AUTODESK INVENTOR PART (.ipt)
format: ipt  version: 2015 (Build 190159000, 159)  size: 509,952 bytes
history: native  units: mm
features: other x19, loft x3, pattern_circular x3, sketch x1
ambient origin geometry x6: Origin, XZ Plane, X Axis, Y Axis, Z Axis, Center Point
bodies: Solid1 (feature_tree), 实体草图 (feature_tree)
feature tree (26):
  other  "网格平面 2"
  other  "齿实体"
  other  "齿平面"
  other  "起始草图"
  loft  "Loft"
  pattern_circular  "Circular Pattern"  [2 undecoded]
  other  "三维草图 (右)"
  other  "终止平面 (右)"
  loft  "放样 (右)"
  pattern_circular  "环形阵列 (右)"  [2 undecoded]
  other  "三维草图 (左)"
  other  "终止平面 (左)"
  loft  "放样 (左)"
  pattern_circular  "环形阵列 (左)"  [2 undecoded]
  other  "固定实体"
  other  "网格平面"
  other  "上平面"
  other  "齿实体草图"
  other  "终止平面"
  other  "终止草图"
  other  "Helical Curve Left"
  other  "终止草图 (左)"
  sketch  "Sketch6"  dims[d0=60.0mm d1=54.009238mm d2=64.992302mm d3=21.6mm d4=43.335899mm d5=90.0deg d7=13.347684mm d8=14.546903mm d9=30.486592mm d11=21.93mm d12=7.948735mm d15=8.662887mm d16=18.155197mm d17=0.0mm d18=90.0deg d19=0.0mm d20=90.0deg d21=200.0mm d22=360.0deg d26=344.859308mm d27=18.246863mm d28=60.0mm d29=-5.880026mm d30=7.948735mm d31=8.662887mm d32=18.155197mm d35=0.0mm d37=0.0mm d39=0.0mm d40=90.0deg d41=200.0mm d42=360.0deg d46=90.0deg d47=90.0deg d48=0.0mm d49=0.0mm d50=90.0deg d51=1.570796mm d52=0.0mm d53=0.0mm d54=0.0mm d56=16.241168mm d57=41.035513mm d58=31.663513mm d59=24.437229mm d60=18.85607mm d61=24.437229mm d62=18.85607mm d65=344.859308mm d66=31.5mm d67=60.0mm d68=-5.880026mm d69=18.246863mm d70=8.662887mm d71=18.155197mm d72=7.948735mm d73=18.85607mm d74=24.437229mm d75=0.0mm d77=0.0mm d79=0.0mm d80=90.0deg d81=200.0mm d82=360.0deg d84=10.0mm d85=20.0mm d86=20.0mm d87=10.0mm d88=0.0mm d89=0.0mm d90=90.0deg d91=90.0deg d92=90.0deg d93=90.0deg]
  other  "Srf1"
  other  "Helical Curve Right"
  other  "终止草图 (右)"
note: 6 required parameter values undecoded (feature->parameter linkage not recoverable at this tier; creation-order binding heuristic only, values carry confidence <= 0.55)
